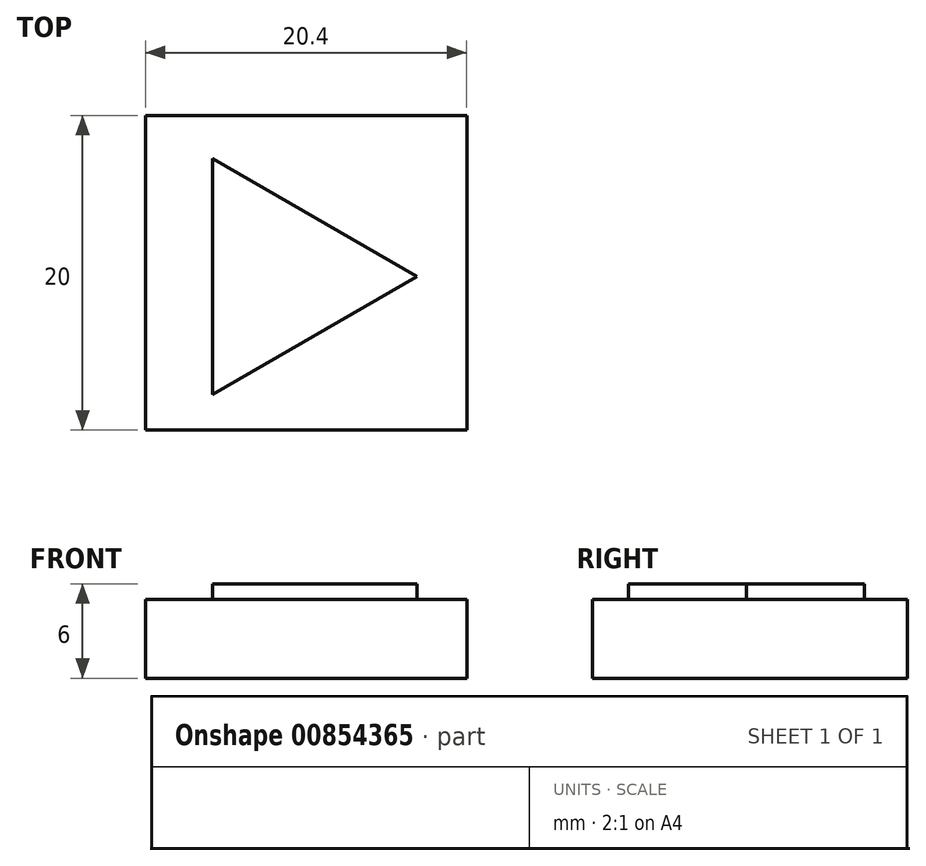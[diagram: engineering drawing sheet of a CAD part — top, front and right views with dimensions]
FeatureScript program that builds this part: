
annotation { "Feature Type Name" : "Feature", "Feature Type Description" : "" }
export const myFeature = defineFeature(function(context is Context, id is Id, definition is map)
    precondition{}
    {
        {
            var Q0;
            Q0=qCreatedBy(makeId("Top.planeOp"),FACE);
            var sketch = newSketch(context, id + "F0", { "sketchPlane" : qUnion([Q0])});
            skLineSegment(sketch, "E0", {"start": v(-18.4, 20) * mm, "end": v(2, 20) * mm});
            skLineSegment(sketch, "E1", {"start": v(-18.4, 20) * mm, "end": v(-18.4, 0) * mm});
            skLineSegment(sketch, "E2", {"start": v(-18.4, 0) * mm, "end": v(2, 0) * mm});
            skLineSegment(sketch, "E3", {"start": v(2, 0) * mm, "end": v(2, 20) * mm});
            skPoint(sketch, "E4.startSnap0", {"position": v(-8.2, 20) * mm});
            skLineSegment(sketch, "E5", {"start": v(-14.15, 17.26) * mm, "end": v(-14.15, 2.26) * mm});
            skLineSegment(sketch, "E6", {"start": v(-14.15, 17.26) * mm, "end": v(-1.16, 9.76) * mm});
            skPoint(sketch, "E6.endSnap0", {"position": v(-14.15, 9.76) * mm});
            skLineSegment(sketch, "E7", {"start": v(-1.16, 9.76) * mm, "end": v(-14.15, 2.26) * mm});
            skSolve(sketch);
        }
        {
            var Q0;
            Q0=makeQuery(id+"F0.imprint","IMPRINT",FACE,{"disambiguationData":[TD([[makeQuery(id+"F0.imprint","IMPRINT",EDGE,{"derivedFrom":sQuery(id+"F0.wireOp",EDGE,"E5")}),1.0]])]});
            extrude(context, id + "F1", {"entities" : qUnion([Q0]), "depth" : 6 * mm, "offsetDistance" : 25 * mm});
        }
        {
            var Q0;
            Q0=makeQuery(id+"F0.imprint","IMPRINT",FACE,{"disambiguationData":[TD([[makeQuery(id+"F0.imprint","IMPRINT",EDGE,{"derivedFrom":sQuery(id+"F0.wireOp",EDGE,"E0")}),-1.0]])]});
            extrude(context, id + "F2", {"entities" : qUnion([Q0]), "operationType" : NewBodyOperationType.ADD, "depth" : 5 * mm, "offsetDistance" : 25 * mm});
        }
    });
